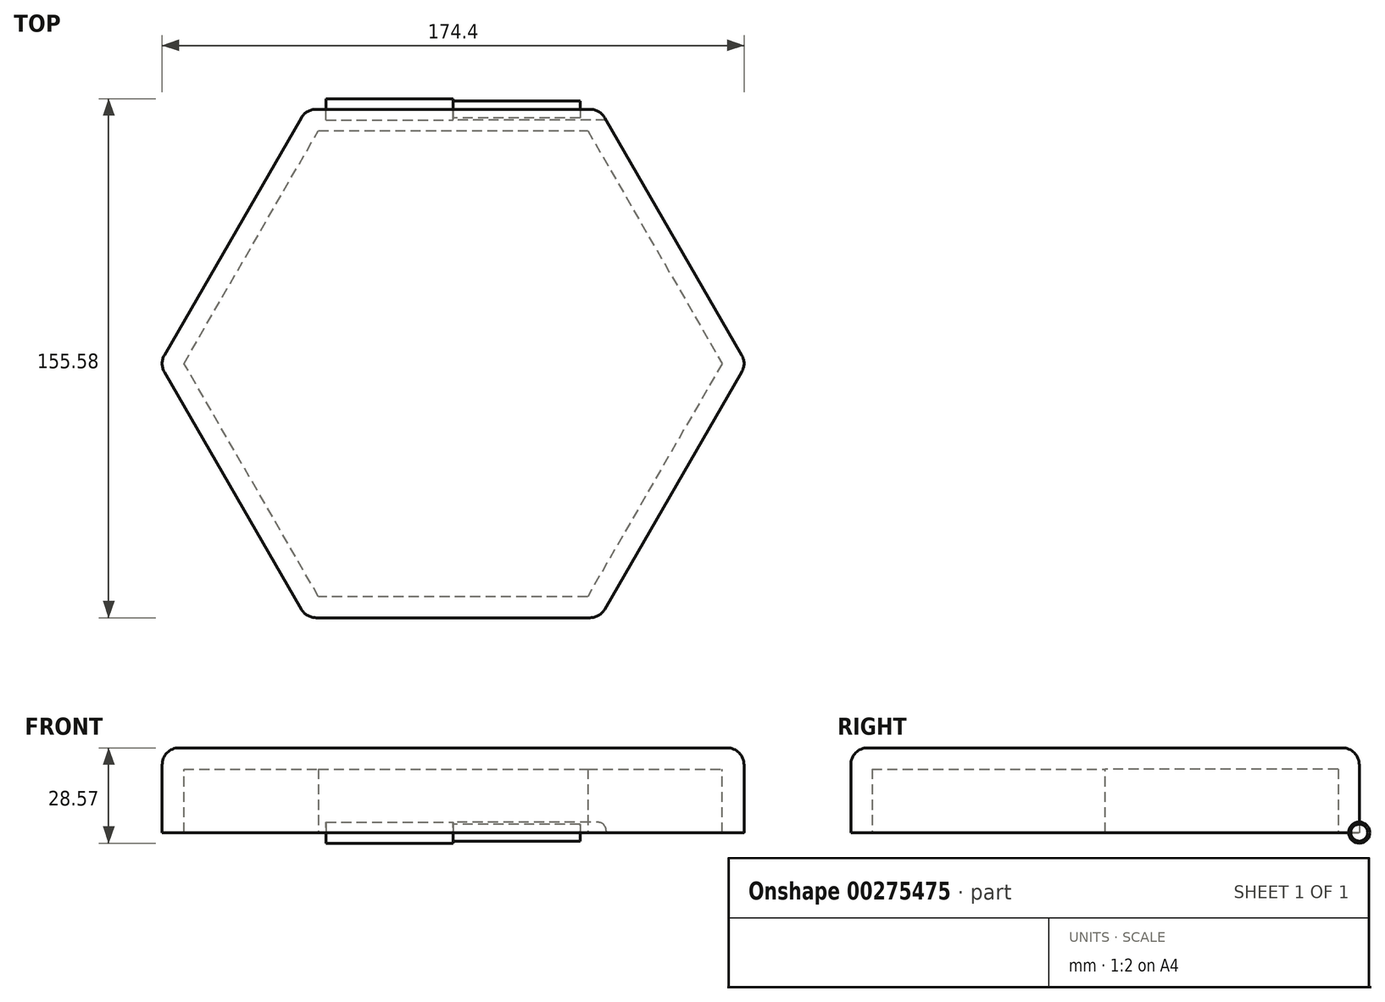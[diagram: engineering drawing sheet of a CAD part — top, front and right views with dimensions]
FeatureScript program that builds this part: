
annotation { "Feature Type Name" : "Feature", "Feature Type Description" : "" }
export const myFeature = defineFeature(function(context is Context, id is Id, definition is map)
    precondition{}
    {
        {
            var Q0;
            Q0=qCreatedBy(makeId("Top.planeOp"),FACE);
            var sketch = newSketch(context, id + "F0", { "sketchPlane" : qUnion([Q0])});
            skCircle(sketch, "E0.cCircle", {"center": v(0, 0) * mm, "radius": 76.2 * mm, "construction": true});
            skLineSegment(sketch, "E0.0", {"start": v(44, -76.2) * mm, "end": v(-44, -76.2) * mm});
            skLineSegment(sketch, "E0.1", {"start": v(-44, -76.2) * mm, "end": v(-87.99, 0) * mm});
            skLineSegment(sketch, "E0.2", {"start": v(-87.99, 0) * mm, "end": v(-44, 76.2) * mm});
            skLineSegment(sketch, "E0.3", {"start": v(-44, 76.2) * mm, "end": v(44, 76.2) * mm});
            skLineSegment(sketch, "E0.4", {"start": v(44, 76.2) * mm, "end": v(87.99, 0) * mm});
            skLineSegment(sketch, "E0.5", {"start": v(87.99, 0) * mm, "end": v(44, -76.2) * mm});
            skPoint(sketch, "E0.0.midPoint", {"position": v(0, -76.2) * mm});
            skSolve(sketch);
        }
        {
            var Q0;
            Q0 = qSketchRegion(id + "F0", true);
            extrude(context, id + "F1", {"entities" : qUnion([Q0]), "depth" : 25.4 * mm});
        }
        {
            var Q0;
            Q0=makeQuery(id+"F1.opExtrude","CAP_FACE",FACE,{"disambiguationData":[OSD([sQuery(id+"F0.wireOp",EDGE,"E0.0"),sQuery(id+"F0.wireOp",EDGE,"E0.1"),sQuery(id+"F0.wireOp",EDGE,"E0.2"),sQuery(id+"F0.wireOp",EDGE,"E0.3"),sQuery(id+"F0.wireOp",EDGE,"E0.4"),sQuery(id+"F0.wireOp",EDGE,"E0.5")])],"isStart":false});
            var Q1;
            Q1=makeQuery(id+"F1.opExtrude","SWEPT_EDGE",EDGE,{"disambiguationData":[OSD([sQuery(id+"F0.wireOp",EDGE,"E0.0"),sQuery(id+"F0.wireOp",EDGE,"E0.5")])]});
            var Q2;
            Q2=makeQuery(id+"F1.opExtrude","SWEPT_EDGE",EDGE,{"disambiguationData":[OSD([sQuery(id+"F0.wireOp",EDGE,"E0.4"),sQuery(id+"F0.wireOp",EDGE,"E0.5")])]});
            var Q3;
            Q3=makeQuery(id+"F1.opExtrude","SWEPT_EDGE",EDGE,{"disambiguationData":[OSD([sQuery(id+"F0.wireOp",EDGE,"E0.0"),sQuery(id+"F0.wireOp",EDGE,"E0.1")])]});
            var Q4;
            Q4=makeQuery(id+"F1.opExtrude","SWEPT_EDGE",EDGE,{"disambiguationData":[OSD([sQuery(id+"F0.wireOp",EDGE,"E0.3"),sQuery(id+"F0.wireOp",EDGE,"E0.4")])]});
            var Q5;
            Q5=makeQuery(id+"F1.opExtrude","SWEPT_EDGE",EDGE,{"disambiguationData":[OSD([sQuery(id+"F0.wireOp",EDGE,"E0.2"),sQuery(id+"F0.wireOp",EDGE,"E0.3")])]});
            var Q6;
            Q6=makeQuery(id+"F1.opExtrude","SWEPT_EDGE",EDGE,{"disambiguationData":[OSD([sQuery(id+"F0.wireOp",EDGE,"E0.1"),sQuery(id+"F0.wireOp",EDGE,"E0.2")])]});
            fillet(context, id + "F2", {"entities" : qUnion([Q0, Q1, Q2, Q3, Q4, Q5, Q6]), "radius" : 5.08 * mm, "tangentPropagation" : true, "allowEdgeOverflow" : false});
        }
        {
            var Q0;
            Q0=makeQuery(id+"F1.opExtrude","CAP_FACE",FACE,{"disambiguationData":[OSD([sQuery(id+"F0.wireOp",EDGE,"E0.0"),sQuery(id+"F0.wireOp",EDGE,"E0.1"),sQuery(id+"F0.wireOp",EDGE,"E0.2"),sQuery(id+"F0.wireOp",EDGE,"E0.3"),sQuery(id+"F0.wireOp",EDGE,"E0.4"),sQuery(id+"F0.wireOp",EDGE,"E0.5")])],"isStart":true});
            shell(context, id + "F3", {"entities" : qUnion([Q0]), "thickness" : 6.35 * mm});
        }
        {
            var Q0;
            Q0=qCreatedBy(makeId("Right.planeOp"),FACE);
            var sketch = newSketch(context, id + "F4", { "sketchPlane" : qUnion([Q0])});
            skCircle(sketch, "E1", {"center": v(76.2, 0) * mm, "radius": 3.18 * mm});
            skSolve(sketch);
        }
        {
            var Q0;
            Q0 = qSketchRegion(id + "F4", true);
            extrude(context, id + "F5", {"entities" : qUnion([Q0]), "operationType" : NewBodyOperationType.ADD, "oppositeDirection" : true, "depth" : 38.1 * mm});
        }
        {
            var Q0;
            Q0=makeQuery(id+"F5.opExtrude","CAP_FACE",FACE,{"disambiguationData":[OSD([sQuery(id+"F4.wireOp",EDGE,"E1")])],"isStart":false});
            var sketch = newSketch(context, id + "F6", { "sketchPlane" : qUnion([Q0])});
            skCircle(sketch, "E2", {"center": v(-76.2, 0) * mm, "radius": 2.54 * mm});
            skSolve(sketch);
        }
        {
            var Q0;
            Q0 = qSketchRegion(id + "F6", true);
            var Q1;
            Q1=sQuery(id+"F6.wireOp",EDGE,"E2");
            extrude(context, id + "F7", {"entities" : qUnion([Q0]), "bodyType" : ToolBodyType.SURFACE, "operationType" : NewBodyOperationType.REMOVE, "surfaceEntities" : qUnion([Q1]), "oppositeDirection" : true, "depth" : 25.4 * mm});
        }
        {
            var Q0;
            Q0=makeQuery(id+"F5.opExtrude","CAP_FACE",FACE,{"disambiguationData":[OSD([sQuery(id+"F4.wireOp",EDGE,"E1")])],"isStart":true});
            extrude(context, id + "F8", {"entities" : qUnion([Q0]), "operationType" : NewBodyOperationType.REMOVE, "endBound" : BoundingType.THROUGH_ALL, "depth" : 25.4 * mm});
        }
        {
            var Q0;
            Q0=makeQuery(id+"F5.opExtrude","CAP_FACE",FACE,{"disambiguationData":[OSD([sQuery(id+"F4.wireOp",EDGE,"E1")])],"isStart":true});
            var sketch = newSketch(context, id + "F9", { "sketchPlane" : qUnion([Q0])});
            skCircle(sketch, "E3", {"center": v(76.2, 0) * mm, "radius": 3.18 * mm});
            skSolve(sketch);
        }
        {
            var Q0;
            Q0 = qSketchRegion(id + "F9", true);
            extrude(context, id + "F10", {"entities" : qUnion([Q0]), "operationType" : NewBodyOperationType.REMOVE, "endBound" : BoundingType.THROUGH_ALL, "depth" : 25.4 * mm});
        }
        {
            var Q0;
            Q0=makeQuery(id+"F10.boolean.opBoolean","MERGE",FACE,{"derivedFrom":[makeQuery(id+"F5.opExtrude","CAP_FACE",FACE,{"disambiguationData":[OSD([sQuery(id+"F4.wireOp",EDGE,"E1")])],"isStart":true}),makeQuery(id+"F10.opExtrude","CAP_FACE",FACE,{"disambiguationData":[OSD([sQuery(id+"F9.wireOp",EDGE,"E3")])],"isStart":true})]});
            var sketch = newSketch(context, id + "F11", { "sketchPlane" : qUnion([Q0])});
            skCircle(sketch, "E4", {"center": v(76.2, 0) * mm, "radius": 2.54 * mm});
            skSolve(sketch);
        }
        {
            var Q0;
            Q0 = qSketchRegion(id + "F11", true);
            extrude(context, id + "F12", {"entities" : qUnion([Q0]), "operationType" : NewBodyOperationType.ADD, "depth" : 38.1 * mm});
        }
    });
